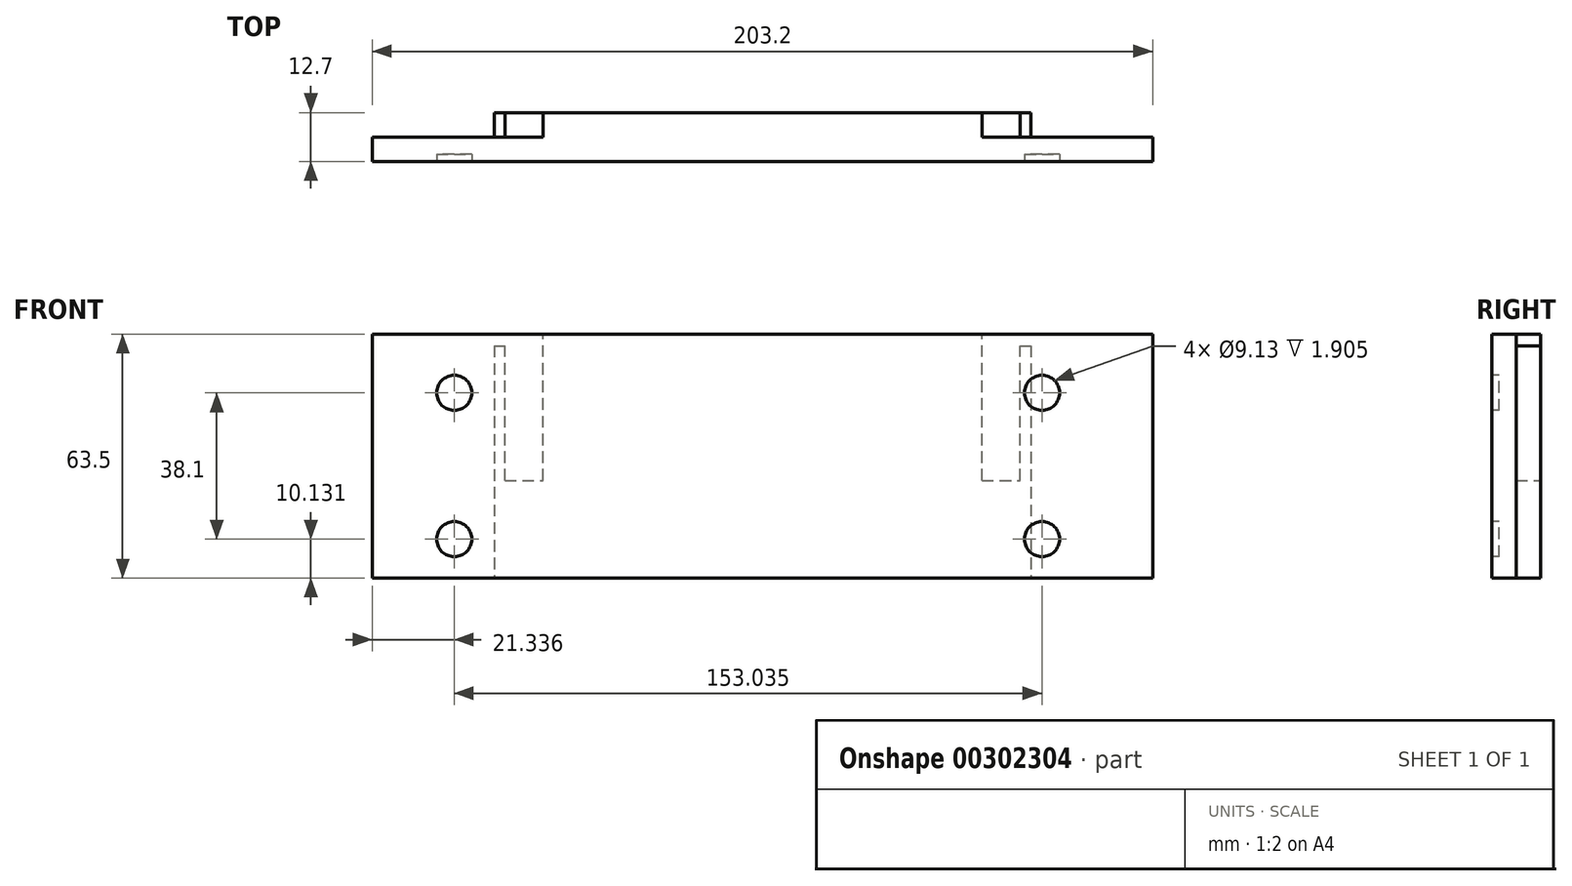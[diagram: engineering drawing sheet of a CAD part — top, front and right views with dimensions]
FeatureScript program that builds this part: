
annotation { "Feature Type Name" : "Feature", "Feature Type Description" : "" }
export const myFeature = defineFeature(function(context is Context, id is Id, definition is map)
    precondition{}
    {
        {
            var Q0;
            Q0=qCreatedBy(makeId("Front.planeOp"),FACE);
            var sketch = newSketch(context, id + "F0", { "sketchPlane" : qUnion([Q0])});
            skLineSegment(sketch, "E0", {"start": v(2.54, 40.87) * mm, "end": v(-99.06, 40.87) * mm});
            skLineSegment(sketch, "E1", {"start": v(2.54, 40.87) * mm, "end": v(104.14, 40.87) * mm});
            skLineSegment(sketch, "E2", {"start": v(2.54, -22.63) * mm, "end": v(104.14, -22.63) * mm});
            skLineSegment(sketch, "E3", {"start": v(104.14, 40.87) * mm, "end": v(104.14, -22.63) * mm});
            skLineSegment(sketch, "E4", {"start": v(-99.06, 40.87) * mm, "end": v(-99.06, -22.63) * mm});
            skLineSegment(sketch, "E5", {"start": v(-99.06, -22.63) * mm, "end": v(2.54, -22.63) * mm});
            skSolve(sketch);
        }
        {
            var Q0;
            Q0=makeQuery(id+"F0.imprint","IMPRINT",FACE,{"disambiguationData":[TD([[makeQuery(id+"F0.imprint","IMPRINT",EDGE,{"derivedFrom":sQuery(id+"F0.wireOp",EDGE,"E0")}),1.0]])]});
            extrude(context, id + "F1", {"entities" : qUnion([Q0]), "depth" : 12.7 * mm, "offsetDistance" : 25.4 * mm});
        }
        {
            var Q0;
            Q0=makeQuery(id+"F1.opExtrude","CAP_FACE",FACE,{"disambiguationData":[OSD([sQuery(id+"F0.wireOp",EDGE,"E0"),sQuery(id+"F0.wireOp",EDGE,"E1"),sQuery(id+"F0.wireOp",EDGE,"E2"),sQuery(id+"F0.wireOp",EDGE,"E3"),sQuery(id+"F0.wireOp",EDGE,"E4"),sQuery(id+"F0.wireOp",EDGE,"E5"),sQuery(id+"F0.wireOp",EDGE,"I3yR4xvX-r2oe-GTPT-vD8Y-mcwfH40HyN0y"),sQuery(id+"F0.wireOp",EDGE,"xT2M75Fc-ZOPW-iyOf-SVoF-M3bb9BzuPpyB"),sQuery(id+"F0.wireOp",EDGE,"CqMDaARp-odtl-oRJk-1PLd-55f6QRkIRfuT"),sQuery(id+"F0.wireOp",EDGE,"FR9P49NI-uUVl-wjhL-mZEc-PBDcwatupjOE")])],"isStart":false});
            var sketch = newSketch(context, id + "F2", { "sketchPlane" : qUnion([Q0])});
            skCircle(sketch, "E6", {"center": v(-77.72, -12.5) * mm, "radius": 4.56 * mm});
            skCircle(sketch, "E7", {"center": v(75.31, -12.5) * mm, "radius": 4.56 * mm});
            skCircle(sketch, "E8", {"center": v(75.31, 25.6) * mm, "radius": 4.56 * mm});
            skCircle(sketch, "E9", {"center": v(-77.72, 25.6) * mm, "radius": 4.56 * mm});
            skSolve(sketch);
        }
        {
            var Q0;
            Q0 = qSketchRegion(id + "F2", true);
            extrude(context, id + "F3", {"entities" : qUnion([Q0]), "operationType" : NewBodyOperationType.REMOVE, "oppositeDirection" : true, "depth" : 1.9 * mm, "offsetDistance" : 25.4 * mm});
        }
        {
            var Q0;
            Q0=makeQuery(id+"F1.opExtrude","CAP_FACE",FACE,{"disambiguationData":[OSD([sQuery(id+"F0.wireOp",EDGE,"E0"),sQuery(id+"F0.wireOp",EDGE,"E1"),sQuery(id+"F0.wireOp",EDGE,"E2"),sQuery(id+"F0.wireOp",EDGE,"E3"),sQuery(id+"F0.wireOp",EDGE,"E4"),sQuery(id+"F0.wireOp",EDGE,"E5")])],"isStart":true});
            var sketch = newSketch(context, id + "F4", { "sketchPlane" : qUnion([Q0])});
            skLineSegment(sketch, "E10", {"start": v(-104.14, 40.87) * mm, "end": v(-72.39, 40.87) * mm});
            skLineSegment(sketch, "E11", {"start": v(-72.4, 40.87) * mm, "end": v(-72.4, -22.63) * mm});
            skLineSegment(sketch, "E12", {"start": v(-72.4, -22.63) * mm, "end": v(-104.14, -22.63) * mm});
            skLineSegment(sketch, "E13", {"start": v(-104.14, 40.87) * mm, "end": v(-104.14, -22.63) * mm});
            skLineSegment(sketch, "E14", {"start": v(99.06, 40.87) * mm, "end": v(67.31, 40.87) * mm});
            skLineSegment(sketch, "E15", {"start": v(67.31, 40.87) * mm, "end": v(67.31, -22.63) * mm});
            skLineSegment(sketch, "E16", {"start": v(67.31, -22.63) * mm, "end": v(99.06, -22.63) * mm});
            skLineSegment(sketch, "E17", {"start": v(99.06, -22.63) * mm, "end": v(99.06, 40.87) * mm});
            skSolve(sketch);
        }
        {
            var Q0;
            Q0=makeQuery(id+"F4.imprint","IMPRINT",FACE,{"disambiguationData":[TD([[makeQuery(id+"F4.imprint","IMPRINT",EDGE,{"derivedFrom":sQuery(id+"F4.wireOp",EDGE,"E10")}),1.0]])]});
            var Q1;
            Q1=makeQuery(id+"F4.imprint","IMPRINT",FACE,{"disambiguationData":[TD([[makeQuery(id+"F4.imprint","IMPRINT",EDGE,{"derivedFrom":sQuery(id+"F4.wireOp",EDGE,"E14")}),1.0]])]});
            extrude(context, id + "F5", {"entities" : qUnion([Q0, Q1]), "operationType" : NewBodyOperationType.REMOVE, "oppositeDirection" : true, "depth" : 6.35 * mm, "offsetDistance" : 25.4 * mm});
        }
        {
            var Q0;
            Q0=makeQuery(id+"F1.opExtrude","SWEPT_FACE",FACE,{"disambiguationData":[OSD([sQuery(id+"F0.wireOp",EDGE,"E0"),sQuery(id+"F0.wireOp",EDGE,"E1")])]});
            var sketch = newSketch(context, id + "F6", { "sketchPlane" : qUnion([Q0])});
            skLineSegment(sketch, "E18", {"start": v(-67.31, -6.35) * mm, "end": v(-54.61, -6.35) * mm});
            skLineSegment(sketch, "E19", {"start": v(72.4, -6.35) * mm, "end": v(59.7, -6.35) * mm});
            skLineSegment(sketch, "E20", {"start": v(59.7, -6.35) * mm, "end": v(59.7, 0) * mm});
            skLineSegment(sketch, "E21", {"start": v(59.7, 0) * mm, "end": v(72.4, 0) * mm});
            skLineSegment(sketch, "E22", {"start": v(72.4, 0) * mm, "end": v(72.4, -6.35) * mm});
            skLineSegment(sketch, "E23", {"start": v(-54.61, -6.35) * mm, "end": v(-54.61, 0) * mm});
            skLineSegment(sketch, "E24", {"start": v(-54.61, 0) * mm, "end": v(-67.31, 0) * mm});
            skLineSegment(sketch, "E25", {"start": v(-67.31, 0) * mm, "end": v(-67.31, -6.35) * mm});
            skLineSegment(sketch, "E26", {"start": v(59.7, -6.35) * mm, "end": v(62.46, -6.35) * mm});
            skLineSegment(sketch, "E27", {"start": v(59.7, 0) * mm, "end": v(62.46, 0) * mm});
            skLineSegment(sketch, "E28", {"start": v(-54.61, -6.35) * mm, "end": v(-57.38, -6.35) * mm});
            skLineSegment(sketch, "E29", {"start": v(-57.38, 0) * mm, "end": v(-54.61, 0) * mm});
            skLineSegment(sketch, "E30", {"start": v(72.4, -6.35) * mm, "end": v(69.62, -6.35) * mm});
            skLineSegment(sketch, "E31", {"start": v(69.62, -6.35) * mm, "end": v(69.62, 0) * mm});
            skLineSegment(sketch, "E32", {"start": v(69.62, 0) * mm, "end": v(59.7, 0) * mm});
            skLineSegment(sketch, "E33", {"start": v(-67.31, -6.35) * mm, "end": v(-64.54, -6.35) * mm});
            skLineSegment(sketch, "E34", {"start": v(-64.54, -6.35) * mm, "end": v(-64.54, 0) * mm});
            skSolve(sketch);
        }
        {
            var Q0;
            Q0 = qSketchRegion(id + "F6", true);
            extrude(context, id + "F7", {"entities" : qUnion([Q0]), "operationType" : NewBodyOperationType.REMOVE, "oppositeDirection" : true, "depth" : 3 * mm, "offsetDistance" : 25.4 * mm});
        }
        {
            var Q0;
            Q0=makeQuery(id+"F6.imprint","IMPRINT",FACE,{"disambiguationData":[TD([[makeQuery(id+"F6.imprint","IMPRINT",EDGE,{"derivedFrom":sQuery(id+"F6.wireOp",EDGE,"E18")}),1.0]])]});
            var Q1;
            Q1=makeQuery(id+"F6.imprint","IMPRINT",FACE,{"disambiguationData":[TD([[makeQuery(id+"F6.imprint","IMPRINT",EDGE,{"derivedFrom":sQuery(id+"F6.wireOp",EDGE,"E19")}),-1.0]])]});
            extrude(context, id + "F8", {"entities" : qUnion([Q0, Q1]), "operationType" : NewBodyOperationType.REMOVE, "oppositeDirection" : true, "depth" : 38.1 * mm, "offsetDistance" : 25.4 * mm});
        }
    });
